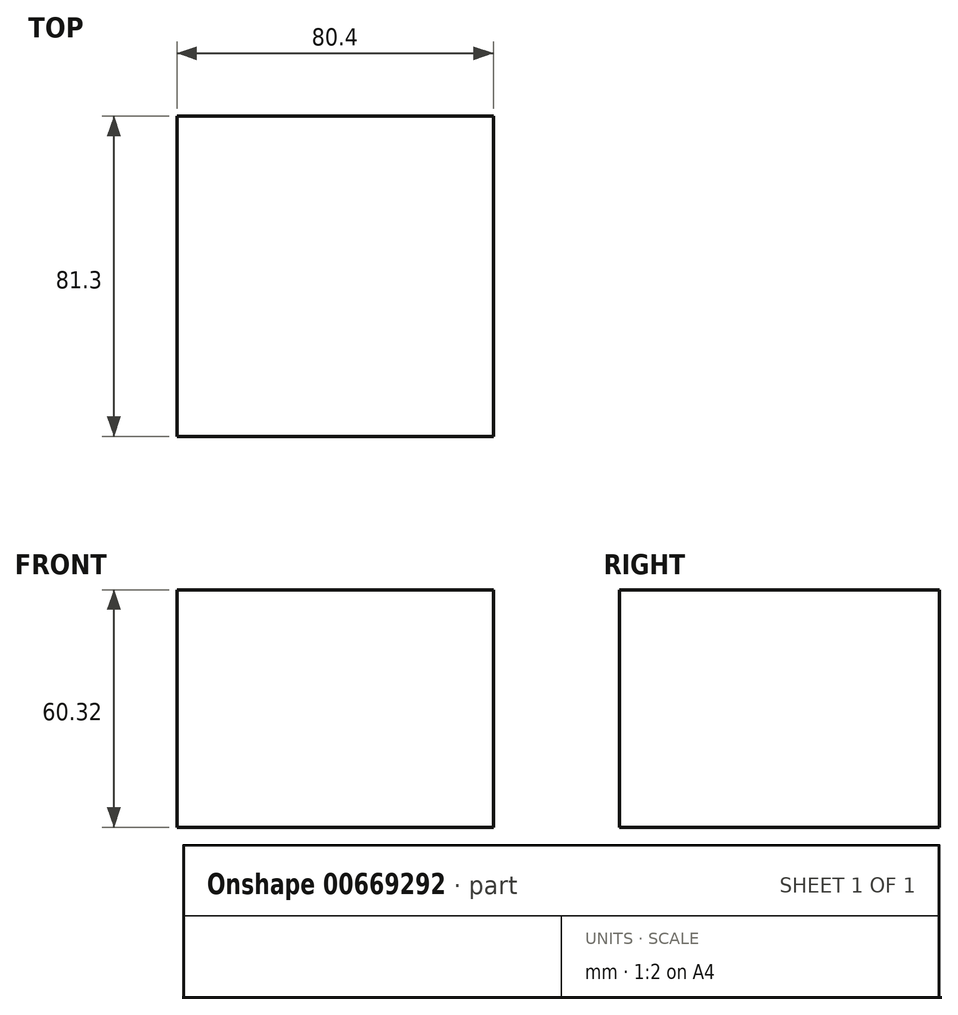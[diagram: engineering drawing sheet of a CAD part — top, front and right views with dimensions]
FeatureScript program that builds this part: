
annotation { "Feature Type Name" : "Feature", "Feature Type Description" : "" }
export const myFeature = defineFeature(function(context is Context, id is Id, definition is map)
    precondition{}
    {
        {
            var Q0;
            Q0=qCreatedBy(makeId("Top.planeOp"),FACE);
            var sketch = newSketch(context, id + "F0", { "sketchPlane" : qUnion([Q0])});
            skLineSegment(sketch, "E0", {"start": v(-40.2, -40.65) * mm, "end": v(-40.2, 40.65) * mm});
            skLineSegment(sketch, "E1", {"start": v(-40.2, 40.65) * mm, "end": v(40.2, 40.65) * mm});
            skLineSegment(sketch, "E2", {"start": v(40.2, 40.65) * mm, "end": v(40.2, -40.65) * mm});
            skLineSegment(sketch, "E3", {"start": v(40.2, -40.65) * mm, "end": v(-40.2, -40.65) * mm});
            skSolve(sketch);
        }
        {
            var Q0;
            Q0 = qSketchRegion(id + "F0", true);
            extrude(context, id + "F1", {"entities" : qUnion([Q0]), "endBound" : BoundingType.SYMMETRIC, "depth" : 60.32 * mm, "offsetDistance" : 25.4 * mm});
        }
    });
